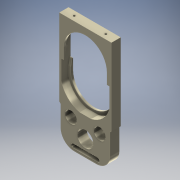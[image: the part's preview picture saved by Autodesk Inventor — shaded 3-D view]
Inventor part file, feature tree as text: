
AUTODESK INVENTOR PART (.ipt)
format: ipt  version: 2016 (Build 200138000, 138)  size: 317,440 bytes
history: native  units: mm
features: extrude x10, sketch x9, chamfer x6, projected_geometry x5, mirror x2, hole x1, thicken_offset x1
ambient origin geometry x8: Origin, YZ Plane, XZ Plane, XY Plane, X Axis, Y Axis, Z Axis, Center Point
bodies: Body1 (feature_tree)
feature tree (34):
  sketch  "Sketch13"  dims[d49=70.0mm d50=62.75mm]
  extrude  "Extrusion11"  Depth=62.75mm
  extrude  "Extrusion12"  Depth=62.75mm
  extrude  "Extrusion13"  Depth=111.0mm
  chamfer  "Chamfer3"  Distance=3.0mm
  chamfer  "Chamfer4"  Distance=10.5mm
  chamfer  "Chamfer5"  Distance=3.0mm
  chamfer  "Chamfer6"  Distance=2.0mm Angle=45.0deg
  chamfer  "Chamfer7"  Distance=10.0mm Angle=45.0deg
  extrude  "Extrusion17"  Depth=2.0mm TaperAngle=45.0deg
  mirror  "Mirror4"
  extrude  "Extrusion14"  Depth=3.0mm TaperAngle=0.0deg
  sketch  "Sketch16"  dims[d68=10.0mm d69=2.0mm d70=45.0deg d71=2.0mm d72=10.0mm d73=45.0deg]
  extrude  "Extrusion20"  Depth=3.0mm
  extrude  "Extrusion21"  Depth=50.0mm TaperAngle=0.0deg
  chamfer  "Chamfer8"  Distance=3.0mm
  extrude  "Extrusion22"  Depth=20.0mm
  extrude  "Extrusion23"  Depth=6.0mm TaperAngle=0.0deg
  mirror  "Mirror5"
  hole  "Hole1"  [1 undecoded]
  extrude  "Extrusion24"  Depth=72.0mm
  thicken_offset  "Thicken2"
  sketch  "Sketch14"  dims[d51=70.0mm d53=62.75mm]
  projected_geometry  "Projected Loop2"
  sketch  "Sketch15"  dims[d54=76.0mm d55=111.0mm d56=3.0mm d57=0.0mm d58=10.5mm d59=0.0mm d60=3.0mm d61=0.0mm d62=2.0mm d63=2.0mm d64=45.0deg d65=10.0mm d66=2.0mm d67=45.0deg]
  projected_geometry  "Projected Loop3"
  sketch  "Sketch21"  dims[d74=2.0mm d75=10.0mm d76=45.0deg d77=3.0mm d78=0.0mm]
  projected_geometry  "Projected Loop5"
  sketch  "Sketch22"  dims[d85=45.0deg d86=3.0mm]
  sketch  "Sketch23"  dims[d87=50.0mm d88=0.0mm d95=50.0mm d96=0.0mm]
  projected_geometry  "Projected Loop6"
  sketch  "Sketch24"  dims[d97=35.0mm]
  projected_geometry  "Projected Loop7"
  sketch  "Sketch25"  dims[d98=3.0mm d99=3.0mm d100=20.0mm d101=6.0mm d102=0.0mm d103=1.0mm d104=2.0mm d105=45.0deg d108=72.0mm d109=10.0mm d110=0.0mm d111=72.0mm d112=10.0mm d113=0.0mm d115=3.0mm d116=6.0mm d117=4.0mm d118=2.0mm d119=90.0deg d120=8.0mm d121=20.594885mm d122=0.2mm d123=0.15mm d124=10.0mm d125=0.0mm d126=23.0mm d127=17.5mm]
note: 1 required parameter value undecoded (feature->parameter linkage not recoverable at this tier; creation-order binding heuristic only, values carry confidence <= 0.55)
